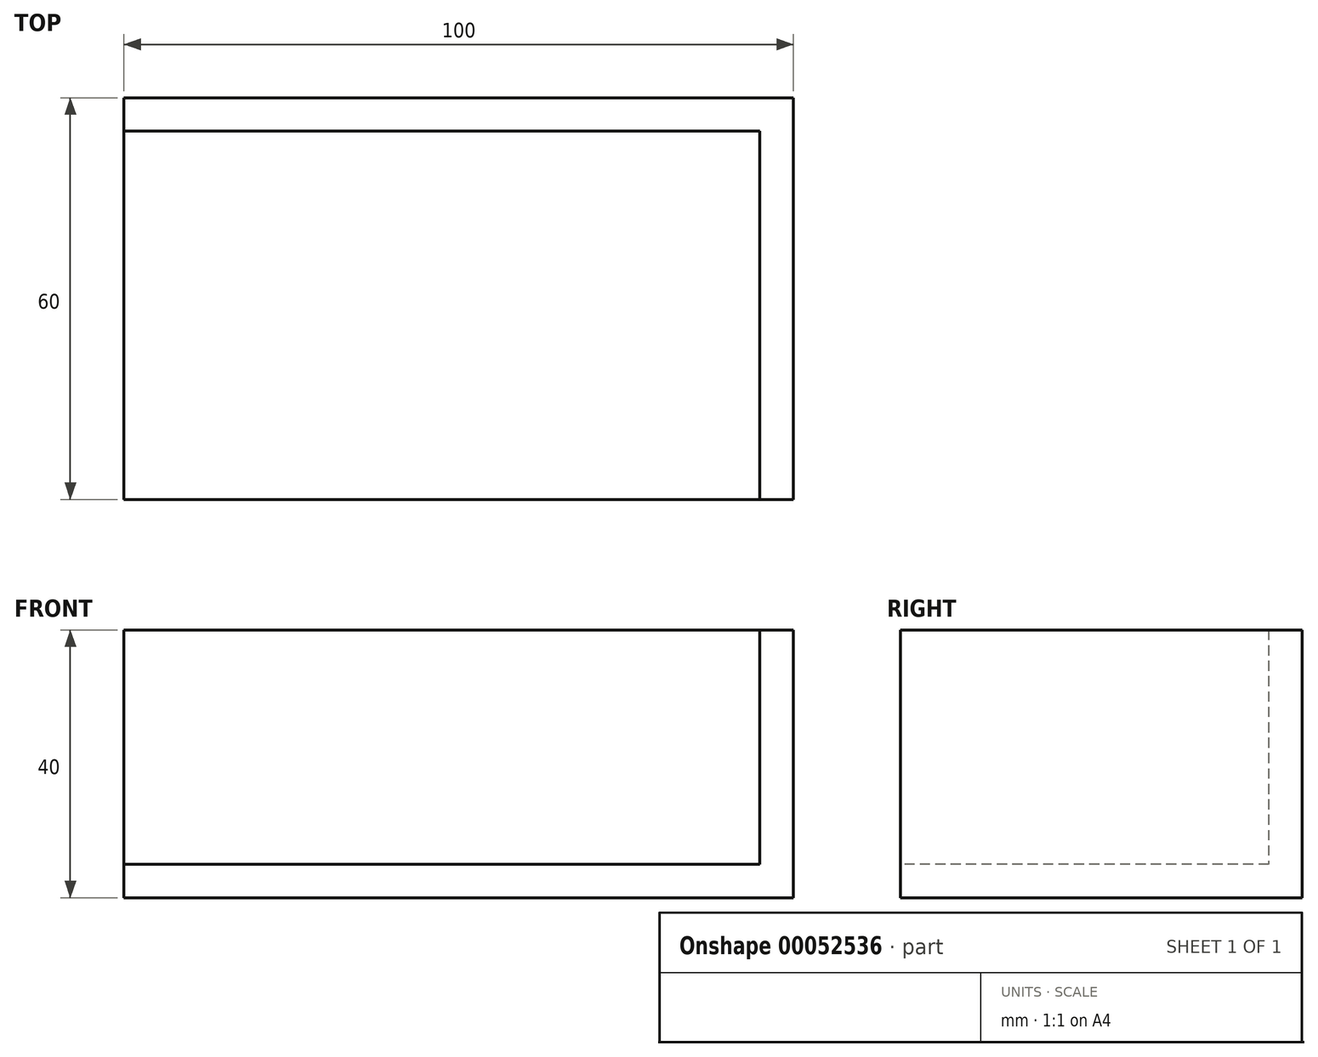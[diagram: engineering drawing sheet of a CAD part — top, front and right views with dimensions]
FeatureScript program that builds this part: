
annotation { "Feature Type Name" : "Feature", "Feature Type Description" : "" }
export const myFeature = defineFeature(function(context is Context, id is Id, definition is map)
    precondition{}
    {
        {
            var Q0;
            Q0=qCreatedBy(makeId("Top.planeOp"),FACE);
            var sketch = newSketch(context, id + "F0", { "sketchPlane" : qUnion([Q0])});
            skLineSegment(sketch, "E0.bottom", {"start": v(-105.53, -22.43) * mm, "end": v(-5.53, -22.43) * mm});
            skLineSegment(sketch, "E0.top", {"start": v(-105.53, -82.43) * mm, "end": v(-5.53, -82.43) * mm});
            skLineSegment(sketch, "E0.left", {"start": v(-105.53, -22.43) * mm, "end": v(-105.53, -82.43) * mm});
            skLineSegment(sketch, "E0.right", {"start": v(-5.53, -22.43) * mm, "end": v(-5.53, -82.43) * mm});
            skSolve(sketch);
        }
        {
            var Q0;
            Q0=makeQuery(id+"F0.imprint","IMPRINT",FACE,{"disambiguationData":[TD([[makeQuery(id+"F0.imprint","IMPRINT",EDGE,{"derivedFrom":sQuery(id+"F0.wireOp",EDGE,"E0.bottom")}),-1.0]])]});
            extrude(context, id + "F1", {"entities" : qUnion([Q0]), "depth" : 5 * mm});
        }
        {
            var Q0;
            Q0=makeQuery(id+"F1.opExtrude","CAP_FACE",FACE,{"disambiguationData":[OSD([sQuery(id+"F0.wireOp",EDGE,"E0.bottom"),sQuery(id+"F0.wireOp",EDGE,"E0.top"),sQuery(id+"F0.wireOp",EDGE,"E0.left"),sQuery(id+"F0.wireOp",EDGE,"E0.right")])],"isStart":false});
            var sketch = newSketch(context, id + "F2", { "sketchPlane" : qUnion([Q0])});
            skLineSegment(sketch, "E1.bottom", {"start": v(-105.53, -22.43) * mm, "end": v(-5.53, -22.43) * mm});
            skLineSegment(sketch, "E1.top", {"start": v(-105.53, -27.43) * mm, "end": v(-5.53, -27.43) * mm});
            skLineSegment(sketch, "E1.left", {"start": v(-105.53, -22.43) * mm, "end": v(-105.53, -27.43) * mm});
            skLineSegment(sketch, "E1.right", {"start": v(-5.53, -22.43) * mm, "end": v(-5.53, -27.43) * mm});
            skLineSegment(sketch, "E2.bottom", {"start": v(-5.53, -22.43) * mm, "end": v(-10.53, -22.43) * mm});
            skLineSegment(sketch, "E2.top", {"start": v(-5.53, -82.43) * mm, "end": v(-10.53, -82.43) * mm});
            skLineSegment(sketch, "E2.left", {"start": v(-5.53, -22.43) * mm, "end": v(-5.53, -82.43) * mm});
            skLineSegment(sketch, "E2.right", {"start": v(-10.53, -22.43) * mm, "end": v(-10.53, -82.43) * mm});
            skSolve(sketch);
        }
        {
            var Q0;
            Q0 = qSketchRegion(id + "F2", true);
            extrude(context, id + "F3", {"entities" : qUnion([Q0]), "operationType" : NewBodyOperationType.ADD, "depth" : 35 * mm});
        }
    });
